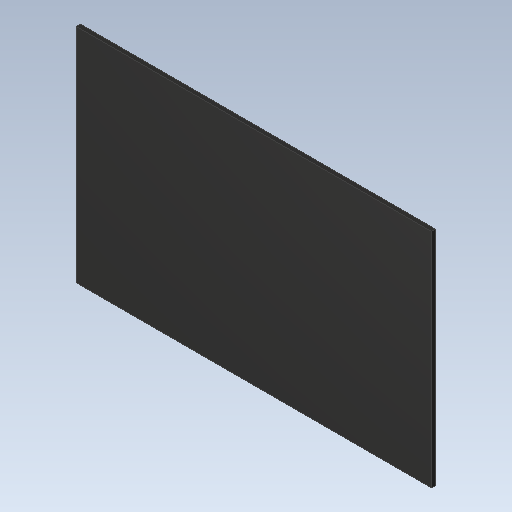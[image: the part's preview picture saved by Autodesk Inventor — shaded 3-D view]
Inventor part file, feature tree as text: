
AUTODESK INVENTOR PART (.ipt)
format: ipt  version: 2023 (Build 270158000, 158)  size: 90,624 bytes
history: imported  units: in
note: dims shown in document units (in); Inventor stores cm internally (conversion verified against a paired STEP export)
features: imported_body x1
ambient origin geometry x8: Origin, YZ Plane, XZ Plane, XY Plane, X Axis, Y Axis, Z Axis, Center Point
bodies: Solid1 (imported_parasolid), Body1 (imported_parasolid)
feature tree (1):
  imported_body  NMx_Import_Brep_tag  [imported B-rep: ~6 faces, bbox_mm=[8.8, 5.5, 0.1]]
